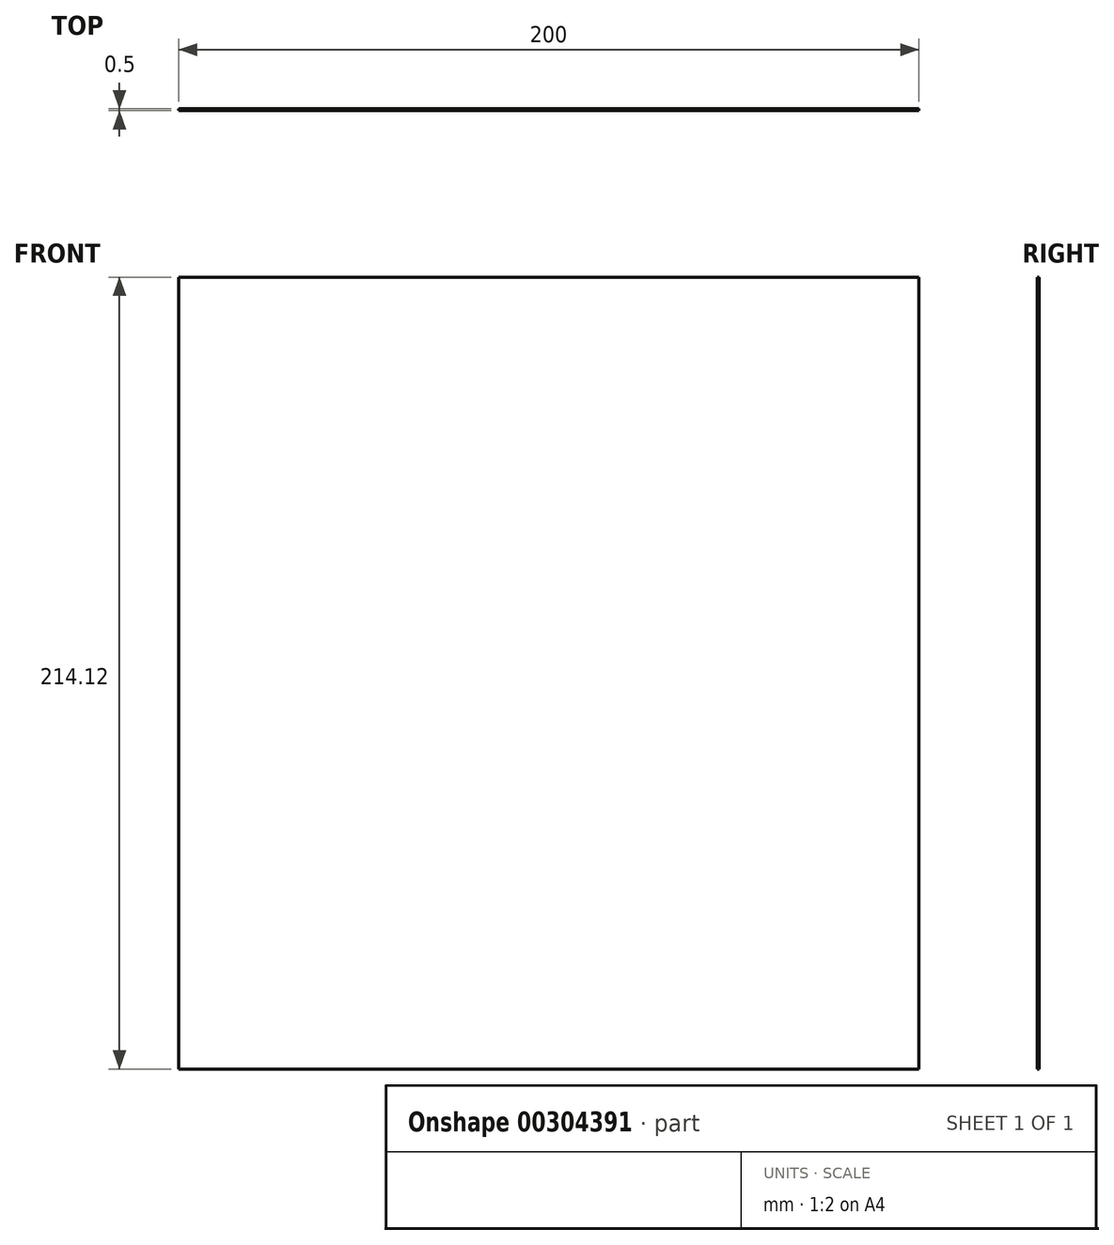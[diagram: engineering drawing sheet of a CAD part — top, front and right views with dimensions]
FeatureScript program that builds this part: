
annotation { "Feature Type Name" : "Feature", "Feature Type Description" : "" }
export const myFeature = defineFeature(function(context is Context, id is Id, definition is map)
    precondition{}
    {
        {
            var Q0;
            Q0=qCreatedBy(makeId("Front.planeOp"),FACE);
            var sketch = newSketch(context, id + "F0", { "sketchPlane" : qUnion([Q0])});
            skLineSegment(sketch, "E0.bottom", {"start": v(100, 107.06) * mm, "end": v(-100, 107.06) * mm});
            skLineSegment(sketch, "E0.top", {"start": v(100, -107.06) * mm, "end": v(-100, -107.06) * mm});
            skLineSegment(sketch, "E0.left", {"start": v(100, 107.06) * mm, "end": v(100, -107.06) * mm});
            skLineSegment(sketch, "E0.right", {"start": v(-100, 107.06) * mm, "end": v(-100, -107.06) * mm});
            skPoint(sketch, "E0.middle", {"position": v(0, 0) * mm});
            skSolve(sketch);
        }
        {
            var Q0;
            Q0=makeQuery(id+"F0.imprint","IMPRINT",FACE,{"disambiguationData":[TD([[makeQuery(id+"F0.imprint","IMPRINT",EDGE,{"derivedFrom":sQuery(id+"F0.wireOp",EDGE,"E0.bottom")}),1.0]])]});
            extrude(context, id + "F1", {"entities" : qUnion([Q0]), "depth" : .5 * mm});
        }
    });
